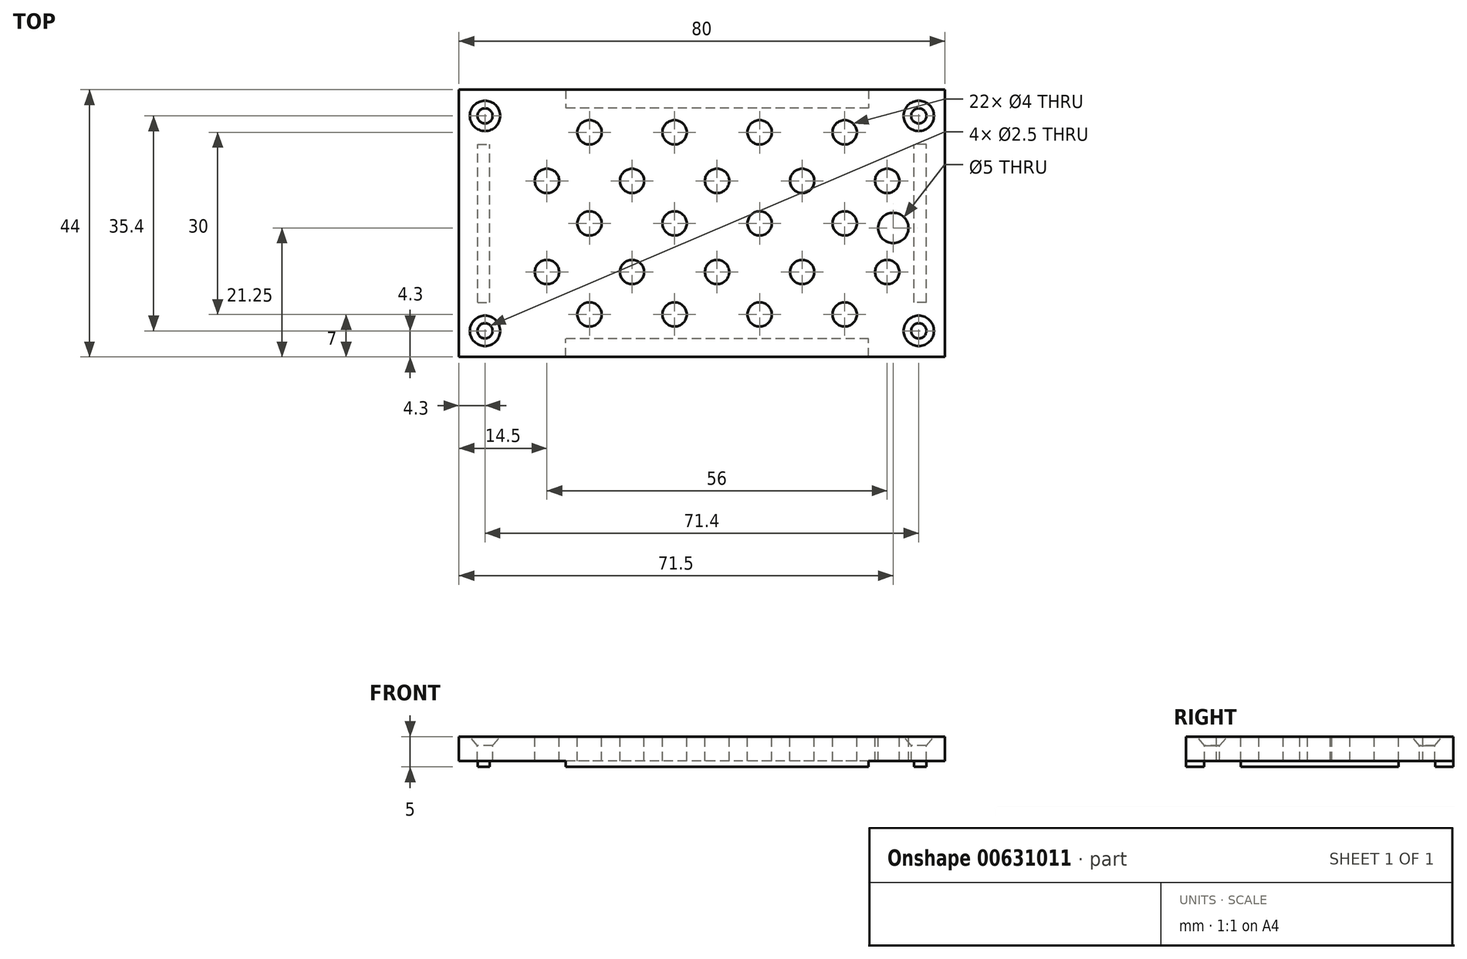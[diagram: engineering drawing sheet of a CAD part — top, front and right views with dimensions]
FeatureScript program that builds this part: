
annotation { "Feature Type Name" : "Feature", "Feature Type Description" : "" }
export const myFeature = defineFeature(function(context is Context, id is Id, definition is map)
    precondition{}
    {
        {
            var Q0;
            Q0=qCreatedBy(makeId("Top.planeOp"),FACE);
            var sketch = newSketch(context, id + "F0", { "sketchPlane" : qUnion([Q0])});
            skLineSegment(sketch, "E0.bottom", {"start": v(-40, 22) * mm, "end": v(40, 22) * mm});
            skLineSegment(sketch, "E0.top", {"start": v(-40, -22) * mm, "end": v(40, -22) * mm});
            skLineSegment(sketch, "E0.left", {"start": v(-40, 22) * mm, "end": v(-40, -22) * mm});
            skLineSegment(sketch, "E0.right", {"start": v(40, 22) * mm, "end": v(40, -22) * mm});
            skPoint(sketch, "E0.middle", {"position": v(0, 0) * mm});
            skSolve(sketch);
        }
        {
            var Q0;
            Q0=makeQuery(id+"F0.imprint","IMPRINT",FACE,{"disambiguationData":[TD([[makeQuery(id+"F0.imprint","IMPRINT",EDGE,{"derivedFrom":sQuery(id+"F0.wireOp",EDGE,"E0.bottom")}),-1.0]])]});
            extrude(context, id + "F1", {"entities" : qUnion([Q0]), "depth" : 4 * mm, "offsetDistance" : 25 * mm});
        }
        {
            var Q0;
            Q0=makeQuery(id+"F1.opExtrude","CAP_FACE",FACE,{"disambiguationData":[OSD([sQuery(id+"F0.wireOp",EDGE,"E0.bottom"),sQuery(id+"F0.wireOp",EDGE,"E0.top"),sQuery(id+"F0.wireOp",EDGE,"E0.left"),sQuery(id+"F0.wireOp",EDGE,"E0.right")])],"isStart":false});
            var sketch = newSketch(context, id + "F2", { "sketchPlane" : qUnion([Q0])});
            skPoint(sketch, "E1", {"position": v(-35.7, -17.7) * mm});
            skPoint(sketch, "E2", {"position": v(35.7, -17.7) * mm});
            skPoint(sketch, "E3", {"position": v(35.7, 17.7) * mm});
            skPoint(sketch, "E4", {"position": v(-35.7, 17.7) * mm});
            skSolve(sketch);
        }
        {
            var Q0;
            Q0=sQuery(id+"F2.wireOp",VERTEX,"E1");
            var Q1;
            Q1=sQuery(id+"F2.wireOp",VERTEX,"E4");
            var Q2;
            Q2=sQuery(id+"F2.wireOp",VERTEX,"E3");
            var Q3;
            Q3=sQuery(id+"F2.wireOp",VERTEX,"E2");
            var Q4;
            Q4=makeQuery(id+"F1.opExtrude","SWEPT_BODY",BODY,{"disambiguationData":[OSD([sQuery(id+"F0.wireOp",EDGE,"E0.bottom"),sQuery(id+"F0.wireOp",EDGE,"E0.top"),sQuery(id+"F0.wireOp",EDGE,"E0.left"),sQuery(id+"F0.wireOp",EDGE,"E0.right")])]});
            hole(context, id + "F3", {"style" : HoleStyle.C_SINK, "endStyle" : HoleEndStyle.BLIND, "holeDiameter" : 2.5 * mm, "cSinkDiameter" : 5 * mm, "cSinkAngle" : 81 * degree, "majorDiameter" : 5 * mm, "holeDepth" : 10 * mm, "isTappedThrough" : true, "tappedDepth" : 12 * mm, "tapClearance" : 3, "locations" : qUnion([Q0, Q1, Q2, Q3]), "scope" : qUnion([Q4])});
        }
        {
            var Q0;
            Q0=makeQuery(id+"F1.opExtrude","CAP_FACE",FACE,{"disambiguationData":[OSD([sQuery(id+"F0.wireOp",EDGE,"E0.bottom"),sQuery(id+"F0.wireOp",EDGE,"E0.top"),sQuery(id+"F0.wireOp",EDGE,"E0.left"),sQuery(id+"F0.wireOp",EDGE,"E0.right")])],"isStart":false});
            var sketch = newSketch(context, id + "F4", { "sketchPlane" : qUnion([Q0])});
            skPoint(sketch, "E5", {"position": v(23.5, -15) * mm});
            skPoint(sketch, "E6", {"position": v(9.5, -15) * mm});
            skPoint(sketch, "E7", {"position": v(-4.5, -15) * mm});
            skPoint(sketch, "E8", {"position": v(-18.5, -15) * mm});
            skPoint(sketch, "E9", {"position": v(-11.5, -8) * mm});
            skPoint(sketch, "E10", {"position": v(-18.5, 0) * mm});
            skPoint(sketch, "E11", {"position": v(-18.5, 15) * mm});
            skPoint(sketch, "E12", {"position": v(-11.5, 7) * mm});
            skPoint(sketch, "E13", {"position": v(2.5, 7) * mm});
            skPoint(sketch, "E14", {"position": v(2.5, -8) * mm});
            skPoint(sketch, "E15", {"position": v(-25.5, -8) * mm});
            skPoint(sketch, "E16", {"position": v(-25.5, 7) * mm});
            skPoint(sketch, "E17", {"position": v(-4.5, 15) * mm});
            skPoint(sketch, "E18", {"position": v(9.5, 15) * mm});
            skPoint(sketch, "E19", {"position": v(23.5, 15) * mm});
            skPoint(sketch, "E20", {"position": v(16.5, 7) * mm});
            skPoint(sketch, "E21", {"position": v(30.5, 7) * mm});
            skPoint(sketch, "E22", {"position": v(-4.5, 0) * mm});
            skPoint(sketch, "E23", {"position": v(9.5, 0) * mm});
            skPoint(sketch, "E24", {"position": v(23.5, 0) * mm});
            skPoint(sketch, "E25", {"position": v(16.5, -8) * mm});
            skPoint(sketch, "E26", {"position": v(30.5, -8) * mm});
            skSolve(sketch);
        }
        {
            var Q0;
            Q0=sQuery(id+"F4.wireOp",VERTEX,"E11");
            var Q1;
            Q1=sQuery(id+"F4.wireOp",VERTEX,"E17");
            var Q2;
            Q2=sQuery(id+"F4.wireOp",VERTEX,"E18");
            var Q3;
            Q3=sQuery(id+"F4.wireOp",VERTEX,"E19");
            var Q4;
            Q4=sQuery(id+"F4.wireOp",VERTEX,"E16");
            var Q5;
            Q5=sQuery(id+"F4.wireOp",VERTEX,"E12");
            var Q6;
            Q6=sQuery(id+"F4.wireOp",VERTEX,"E13");
            var Q7;
            Q7=sQuery(id+"F4.wireOp",VERTEX,"E20");
            var Q8;
            Q8=sQuery(id+"F4.wireOp",VERTEX,"E21");
            var Q9;
            Q9=sQuery(id+"F4.wireOp",VERTEX,"E10");
            var Q10;
            Q10=sQuery(id+"F4.wireOp",VERTEX,"E22");
            var Q11;
            Q11=sQuery(id+"F4.wireOp",VERTEX,"E23");
            var Q12;
            Q12=sQuery(id+"F4.wireOp",VERTEX,"E24");
            var Q13;
            Q13=sQuery(id+"F4.wireOp",VERTEX,"E15");
            var Q14;
            Q14=sQuery(id+"F4.wireOp",VERTEX,"E9");
            var Q15;
            Q15=sQuery(id+"F4.wireOp",VERTEX,"E14");
            var Q16;
            Q16=sQuery(id+"F4.wireOp",VERTEX,"E25");
            var Q17;
            Q17=sQuery(id+"F4.wireOp",VERTEX,"E26");
            var Q18;
            Q18=sQuery(id+"F4.wireOp",VERTEX,"E8");
            var Q19;
            Q19=sQuery(id+"F4.wireOp",VERTEX,"E7");
            var Q20;
            Q20=sQuery(id+"F4.wireOp",VERTEX,"E6");
            var Q21;
            Q21=sQuery(id+"F4.wireOp",VERTEX,"E5");
            var Q22;
            Q22=makeQuery(id+"F1.opExtrude","SWEPT_BODY",BODY,{"disambiguationData":[OSD([sQuery(id+"F0.wireOp",EDGE,"E0.bottom"),sQuery(id+"F0.wireOp",EDGE,"E0.top"),sQuery(id+"F0.wireOp",EDGE,"E0.left"),sQuery(id+"F0.wireOp",EDGE,"E0.right")])]});
            hole(context, id + "F5", {"style" : HoleStyle.SIMPLE, "endStyle" : HoleEndStyle.BLIND, "holeDiameter" : 4 * mm, "majorDiameter" : 5 * mm, "holeDepth" : 10 * mm, "isTappedThrough" : true, "tappedDepth" : 12 * mm, "tapClearance" : 3, "locations" : qUnion([Q0, Q1, Q2, Q3, Q4, Q5, Q6, Q7, Q8, Q9, Q10, Q11, Q12, Q13, Q14, Q15, Q16, Q17, Q18, Q19, Q20, Q21]), "scope" : qUnion([Q22])});
        }
        {
            var Q0;
            Q0=makeQuery(id+"F1.opExtrude","CAP_FACE",FACE,{"disambiguationData":[OSD([sQuery(id+"F0.wireOp",EDGE,"E0.bottom"),sQuery(id+"F0.wireOp",EDGE,"E0.top"),sQuery(id+"F0.wireOp",EDGE,"E0.left"),sQuery(id+"F0.wireOp",EDGE,"E0.right")])],"isStart":false});
            var sketch = newSketch(context, id + "F6", { "sketchPlane" : qUnion([Q0])});
            skPoint(sketch, "E27", {"position": v(31.5, -0.75) * mm});
            skSolve(sketch);
        }
        {
            var Q0;
            Q0=sQuery(id+"F6.wireOp",VERTEX,"E27");
            var Q1;
            Q1=makeQuery(id+"F1.opExtrude","SWEPT_BODY",BODY,{"disambiguationData":[OSD([sQuery(id+"F0.wireOp",EDGE,"E0.bottom"),sQuery(id+"F0.wireOp",EDGE,"E0.top"),sQuery(id+"F0.wireOp",EDGE,"E0.left"),sQuery(id+"F0.wireOp",EDGE,"E0.right")])]});
            hole(context, id + "F7", {"style" : HoleStyle.SIMPLE, "endStyle" : HoleEndStyle.BLIND, "holeDiameter" : 5 * mm, "majorDiameter" : 5 * mm, "holeDepth" : 10 * mm, "isTappedThrough" : true, "tappedDepth" : 12 * mm, "tapClearance" : 3, "locations" : qUnion([Q0]), "scope" : qUnion([Q1])});
        }
        {
            var Q0;
            Q0=makeQuery(id+"F1.opExtrude","CAP_FACE",FACE,{"disambiguationData":[OSD([sQuery(id+"F0.wireOp",EDGE,"E0.bottom"),sQuery(id+"F0.wireOp",EDGE,"E0.top"),sQuery(id+"F0.wireOp",EDGE,"E0.left"),sQuery(id+"F0.wireOp",EDGE,"E0.right")])],"isStart":true});
            var sketch = newSketch(context, id + "F8", { "sketchPlane" : qUnion([Q0])});
            skLineSegment(sketch, "E28.bottom", {"start": v(27.45, 22) * mm, "end": v(-22.45, 22) * mm});
            skLineSegment(sketch, "E28.top", {"start": v(27.45, 19) * mm, "end": v(-22.45, 19) * mm});
            skLineSegment(sketch, "E28.left", {"start": v(27.45, 22) * mm, "end": v(27.45, 19) * mm});
            skLineSegment(sketch, "E28.right", {"start": v(-22.45, 22) * mm, "end": v(-22.45, 19) * mm});
            skLineSegment(sketch, "E29.bottom", {"start": v(27.45, -22) * mm, "end": v(-22.45, -22) * mm});
            skLineSegment(sketch, "E29.top", {"start": v(27.45, -19) * mm, "end": v(-22.45, -19) * mm});
            skLineSegment(sketch, "E29.left", {"start": v(27.45, -22) * mm, "end": v(27.45, -19) * mm});
            skLineSegment(sketch, "E29.right", {"start": v(-22.45, -22) * mm, "end": v(-22.45, -19) * mm});
            skLineSegment(sketch, "E30.bottom", {"start": v(36.93, 13) * mm, "end": v(34.93, 13) * mm});
            skLineSegment(sketch, "E30.top", {"start": v(36.93, -13) * mm, "end": v(34.93, -13) * mm});
            skLineSegment(sketch, "E30.left", {"start": v(36.93, 13) * mm, "end": v(36.93, -13) * mm});
            skLineSegment(sketch, "E30.right", {"start": v(34.93, 13) * mm, "end": v(34.93, -13) * mm});
            skLineSegment(sketch, "E31.bottom", {"start": v(-36.93, 13) * mm, "end": v(-34.93, 13) * mm});
            skLineSegment(sketch, "E31.top", {"start": v(-36.93, -13) * mm, "end": v(-34.93, -13) * mm});
            skLineSegment(sketch, "E31.left", {"start": v(-36.93, 13) * mm, "end": v(-36.93, -13) * mm});
            skLineSegment(sketch, "E31.right", {"start": v(-34.93, 13) * mm, "end": v(-34.93, -13) * mm});
            skSolve(sketch);
        }
        {
            var Q0;
            Q0 = qSketchRegion(id + "F8", true);
            extrude(context, id + "F9", {"entities" : qUnion([Q0]), "operationType" : NewBodyOperationType.ADD, "depth" : 1 * mm, "offsetDistance" : 25 * mm});
        }
    });
